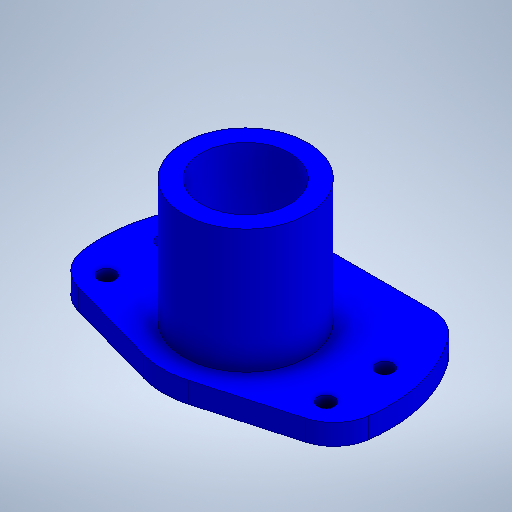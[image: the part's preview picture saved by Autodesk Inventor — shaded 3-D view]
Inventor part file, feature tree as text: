
AUTODESK INVENTOR PART (.ipt)
format: ipt  version: 2025.2 (Build 292293000, 293)  size: 273,920 bytes
history: native  units: mm
features: sketch x2, extrude x2, fillet x1, hole x1
ambient origin geometry x8: Origin, YZ Plane, XZ Plane, XY Plane, X Axis, Y Axis, Z Axis, Center Point
bodies: Solid1 (feature_tree)
feature tree (6):
  sketch  "Sketch1"  dims[d0=70.0mm d1=21.4mm d2=5.0mm d3=0.0mm]
  extrude  "Extrusion1"  Depth=5.0mm
  fillet  "Fillet1"  Radius=5.0mm
  extrude  "Extrusion3"  Depth=2.0mm
  hole  "Hole1"  [1 undecoded]
  sketch  "Sketch3"  dims[d8=48.0mm d9=120.0mm d10=100.0mm d11=100.0mm d12=40.0mm d13=25.0mm d14=10.0mm d15=30.0mm d16=30.0mm d17=0.0mm d18=55.0mm d19=165.0deg d20=4.0mm d21=6.0mm d22=4.0mm d23=2.0mm d24=90.0deg d25=8.0mm d26=20.594885mm]
note: 1 required parameter value undecoded (feature->parameter linkage not recoverable at this tier; creation-order binding heuristic only, values carry confidence <= 0.55)
